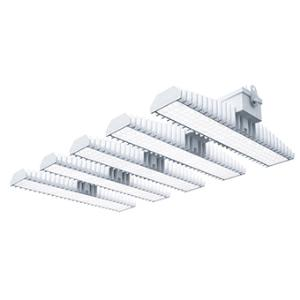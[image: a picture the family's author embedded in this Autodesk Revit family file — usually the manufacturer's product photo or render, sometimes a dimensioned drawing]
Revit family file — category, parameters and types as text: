
# Revit family: 3f_filippi_-_3f_lem_ho_medio_3f_filippi_-_58969_a0812_-_3f_lem_5_ho_led_350_cr_medio___vs_a3b3
name_source: partatom
category: Lighting Fixtures
units: mm (PartAtom-declared; Revit-internal decimal feet)

## family parameters
Cut with Voids When Loaded = No
Host = Face
Light Source = No
Part Type = Normal
Room Calculation Point = No
Round Connector Dimension = Use Diameter
Shared = No

## types (1)
- 3F Filippi - 3F LEM HO Medio (1 x LED, 44794 lm, 345 W, 4000 K)
    Apparent Load = 345 VA
    Approval mark = CE
    CIE Flux Codes = 77 92 98 100 100
    Color Rendering = 80
    Color Temperature = 4000 K
    Control Gear = Electronic ballast
    Default Elevation = 1800 mm
    Description = Industrial luminaire with high light output and high luminous efficiency designed with the most innovative technologies for environments with temperature up to 55°C.

ILLUMINOTECHNICAL
Luminous efficiency 100% (DLOR 98%, ULOR 2%).
Initial luminous flux of the luminaire 44794 lm.
Medium distribution with rectangular shape.
Installation Interdistance Transv.D = 0.87 x hu - Long.D = 0.87 x hu.
Tabular UGR (CIE 117 - 4H-8H; S=0.25H; 70/50/20): RUG 22.2 - 22.2.
Beam angle: 58° - 57°.
Luminous efficacy 130 lm/W.
Lifetime (L93/B10): 30000 h. (tq+25°C)
Lifetime (L90/B10): 50000 h. (tq+25°C)
Lifetime (L85/B10): 80000 h. (tq+25°C)
Lifetime (L80/B10): 100000 h. (tq+25°C)
Lifetime (L85/B10): 50000 h. (tq+55°C)
Sudden decreased luminous flux after 50000 hours: 0% (C0).
Photobiological safety in compliance with IEC/TR 62778: RG0 risk exempt, (IEC 62471).
In compliance with IEC/EN 62722-2-1 - IEC/EN 62717 standards.

SOURCE
5 Mid-Power linear LED modules 70W/840.
Energy efficiency class (UE 2019/2020 - UE 2019/2015): C.
CIE 13.3 Colour rendering index: CRI >80 (R9 <50%).
IES TM-30 Fidelity Index: Rf = 84 Rg = 95.
CCT nominal colour temperature 4000 K.
Colour initial tolerance (MacAdam): SDCM 3.

MECHANICAL
Passive modular heatsinks in die-casted aluminium, painted in white colour.
To optimize the thermal management of the LED module, the heatsinks are oversized and provided with self-cleaning of cooling fins.
Wiring body in aluminium and galvanised steel anchored solidly to the sinks and thermally separated.
3F Lens lenses with high luminous efficiency, transparent methacrylate (PMMA), fixed to the LED modules.
Fixing brackets in stainless steel.
Luminaire with limited surface temperature. - D - (EN 60598-2-24)
Dimensions: 952x542 mm, height 133 mm. Weight 24.08 kg.
IP65 protection degree.
Mechanical strength to impacts IK06 (1 joule).
Glow-wire test resistance 650°C.

ELECTRICAL
Halogen Free electronic wiring 230V-50/60Hz, power factor 0.97, THD <25%, constant output current, class I, 3 driver.
Power of the luminaire 345 W.
ENEC - CE.
SAFE FLICKER: PstLM=<1 and SVM=<0.4 (IEC TR 61547-1 and IEC TR 63158), to ensure a more comfortable and safe light.
Luminaire compliant with EN 60598-2-22 for power supply from a centralised emergency system CPSS (Central Power Supply System), not incorporated in the luminaire - high risk areas excluded. The default power and flux are 100% in AC and 100% in DC.
Ambient temperature from -30°C to +55°C.
Temperature class T6 max 85°C.
Quick connection via M20 3P connector with 9-13 mm tightening range.
Power unit positioned on a separate compartment by the LED module to ensure optimum temperatures of cabling components, to be inspectable and maintainable.
Relative humidity UR: <85%.

INSTALLATION
Ceiling / Suspended / Wall.
All accessories dedicated to this product are available on the Catalog and on our website www.3F-Filippi.com.

ACCESSORIES
A0812 - Anti-glare microprismatic VS moulded glass, tempered, not flammable, with sealing gasket.
One required for each light module. The pack contains 10 pieces.

APPLICATIONS
In commercial environments, exhibition and industrial areas, stores, open areas.
Environments in which it is necessary a total protection against falling fragments (eg environments with foodstuffs or machines with moving parts or with extreme temperature changes), use luminaires with polycarbonate lenses.

WARNING
Fixture not suitable for cold stores with an ambient temperature <0°C and/or relative humidity >85%.
Luminaire designed for disposal/recycling at end-of-life.
Replaceable (LED only) light source by a professional. Replaceable control gear by a professional.
    Height = 133 mm  [stored 0.436352 ft]
    Lamp = 1 x LED
    Lamp Light Flux = 44794 lm
    Lamp Power = 345 W
    Lamp count = 1
    Length = 952 mm
    Lifetime = 50000 h
    Luminous efficacy = 130 lm/W
    Manufacturer = 3F Filippi
    ModVariant = No
    Model = 3F Filippi - 58969+A0812 - 3F LEM 5 HO LED 350 CR MEDIO + VS
    Mounting Place = Ceiling
    Mounting Type = Pendant
    Number of Poles = 1
    OnlyDefault = Yes
    Power Factor = 1
    Product Name = 3F Filippi - 3F LEM HO Medio
    Product group = pendant luminaire
    ProductGroupID = 9
    Protection Class = Protection class I
    Protection Degree = IP 65
    RLX_Detail_Level = 1
    RLX_Emergency_Light_Flux = 0 lm
    RLX_Emergency_Type = 0
    RLX_Emergency_Type_DB = No
    RlxData = <blob elided: 129761 chars, md5=73827fc3>
    Socket = socket
    Standby Power = 0 W
    System Light Flux = 44794 lm
    System Power = 345 W
    Type Comments = Product without accessories
    Type Image = 3f_filippi_-_lem_5__a0812.jpg
    URL = http://relux.com
    VarID = ---
    Voltage = 0 V
    Weight = 0.00 kg
    Width = 542 mm

note: [stored X ft] marks values corroborated as IEEE doubles in the binary element streams (Revit-internal decimal feet)

## geometry (parser evidence)
native form markers: Blend x4, Sweep x13
no freeform markers — native parametric forms only
